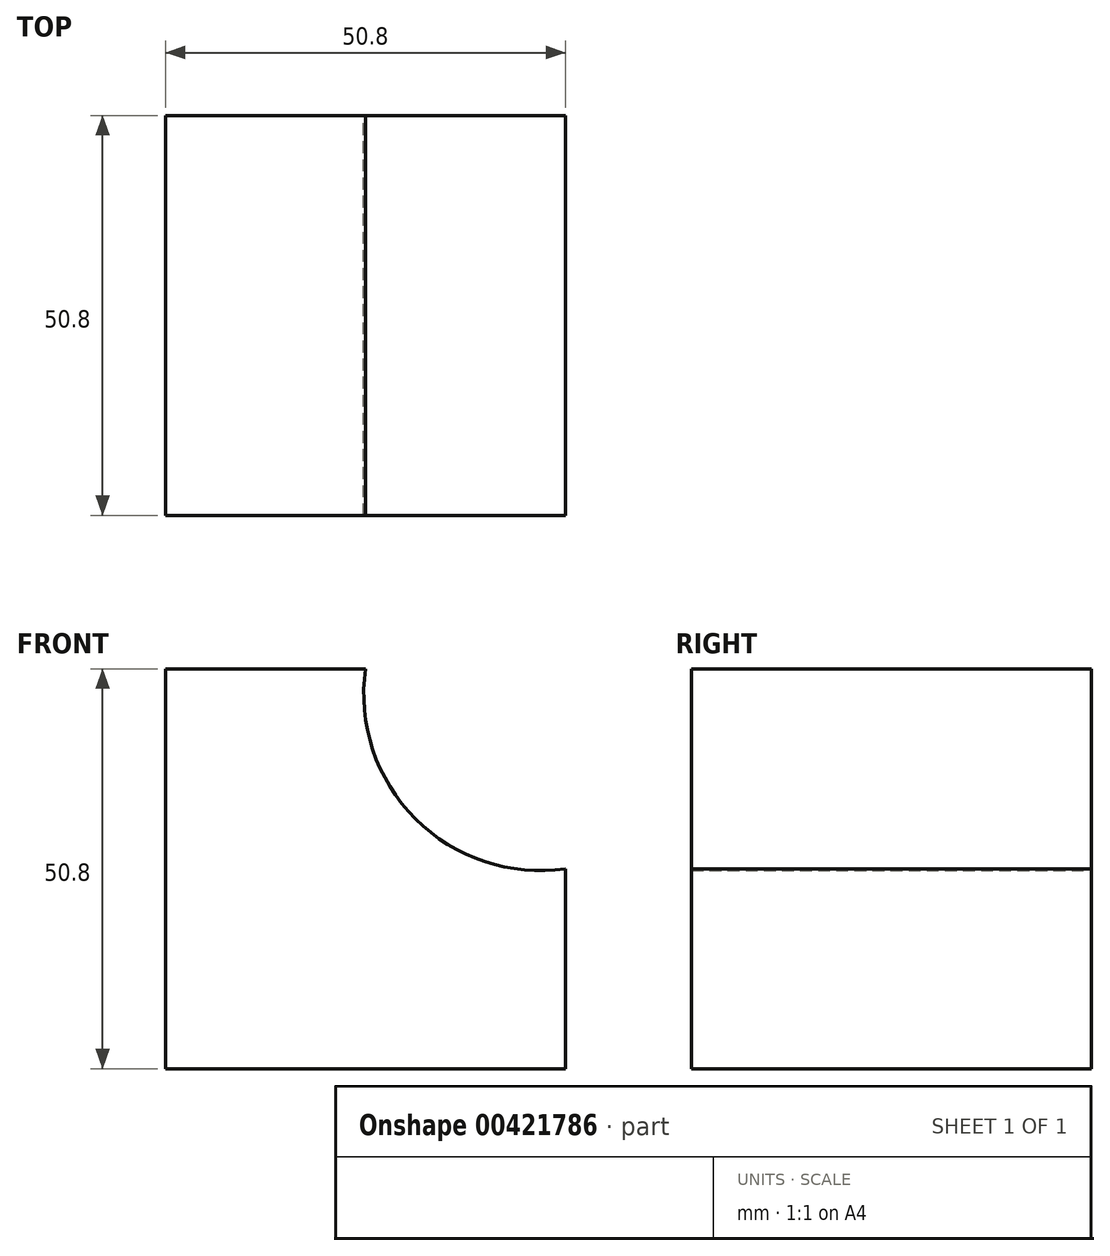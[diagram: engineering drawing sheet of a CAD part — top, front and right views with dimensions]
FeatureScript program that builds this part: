
annotation { "Feature Type Name" : "Feature", "Feature Type Description" : "" }
export const myFeature = defineFeature(function(context is Context, id is Id, definition is map)
    precondition{}
    {
        {
            var Q0;
            Q0=qCreatedBy(makeId("Front.planeOp"),FACE);
            var sketch = newSketch(context, id + "F0", { "sketchPlane" : qUnion([Q0])});
            skLineSegment(sketch, "E0", {"start": v(0, 0) * mm, "end": v(50.8, 0) * mm});
            skLineSegment(sketch, "E1", {"start": v(0, 0) * mm, "end": v(0, 50.8) * mm});
            skLineSegment(sketch, "E2", {"start": v(0, 50.8) * mm, "end": v(25.4, 50.8) * mm});
            skLineSegment(sketch, "E3", {"start": v(50.8, 0) * mm, "end": v(50.8, 25.4) * mm});
            skArc(sketch, "E4", {"start": v(25.4, 50.8) * mm, "mid": v(31.74, 31.74) * mm, "end": v(50.8, 25.4) * mm});
            skSolve(sketch);
        }
        {
            var Q0;
            Q0=makeQuery(id+"F0.imprint","IMPRINT",FACE,{"disambiguationData":[TD([[makeQuery(id+"F0.imprint","IMPRINT",EDGE,{"derivedFrom":sQuery(id+"F0.wireOp",EDGE,"E0")}),1.0]])]});
            extrude(context, id + "F1", {"entities" : qUnion([Q0]), "depth" : 50.8 * mm});
        }
    });
